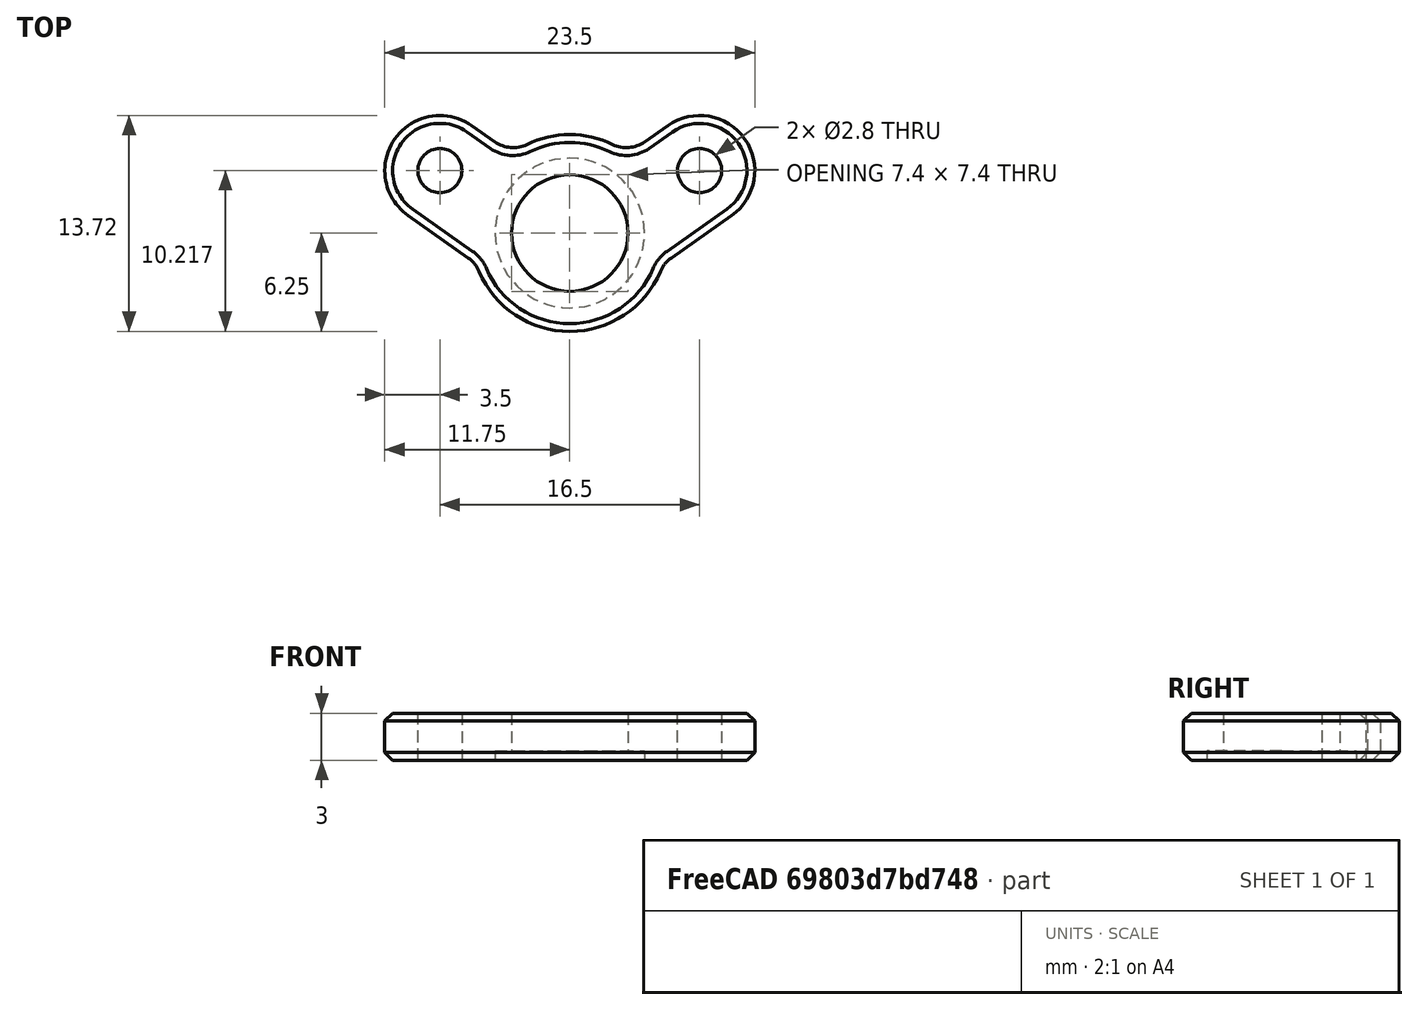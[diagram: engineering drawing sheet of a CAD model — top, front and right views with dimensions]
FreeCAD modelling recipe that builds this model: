
FCSTD DOCUMENT  (FreeCAD 0.18R16146 (Git))
Label: ResizedMikeyMousePart
License: All rights reserved
LicenseURL: http://en.wikipedia.org/wiki/All_rights_reserved
objects: Part::Feature×1, PartDesign::FeatureBase×1, Sketcher::SketchObject×1, PartDesign::Pocket×1, PartDesign::Body×1
note: 6 computed .brp shape members not serialized (recipe doc carries the construction recipe); baked Part::Feature solids carry a one-line shape summary decoded from their .brp

FEATURE [Part::Feature] Part__Feature097  label="三角形连杆轴承压紧件"
  Placement = pos=(111.85,272.442,-106.104) rot=(0,0,-1;0.166228rad)
  shape: bbox 23.27 x 15.03 x 3 mm, 50 faces (baked)
FEATURE [PartDesign::FeatureBase] BaseFeature
  BaseFeature = -> Part__Feature097
FEATURE [Sketcher::SketchObject] Sketch
  ExternalGeometry = -> [BaseFeature]
  MapMode = 5
  Placement = pos=(0,0,3) rot=(0,0,1;0rad)
  Support = -> [BaseFeature]
  sketch-geometry (2):
    g0: Circle CenterX=-8.25 CenterY=3.96712 CenterZ=0 NormalX=0 NormalY=0 NormalZ=1 AngleXU=0 Radius=1.4
    g1: Circle CenterX=8.25 CenterY=3.96712 CenterZ=0 NormalX=0 NormalY=0 NormalZ=1 AngleXU=0 Radius=1.4
  constraints (4):
    c: Coincident(g0,g-4)
    c: Coincident(g1,g-6)
    c: Radius(g1) = 1.4
    c: Radius(g0) = 1.4
FEATURE [PartDesign::Pocket] Pocket
  BaseFeature = -> BaseFeature
  Length = 5
  Length2 = 100
  Profile = -> Sketch
  Type = 1
FEATURE [PartDesign::Body] Body
  BaseFeature = -> Part__Feature097
  Group = -> [BaseFeature,Sketch,Pocket]
  Origin = -> Origin
  Tip = -> Pocket
